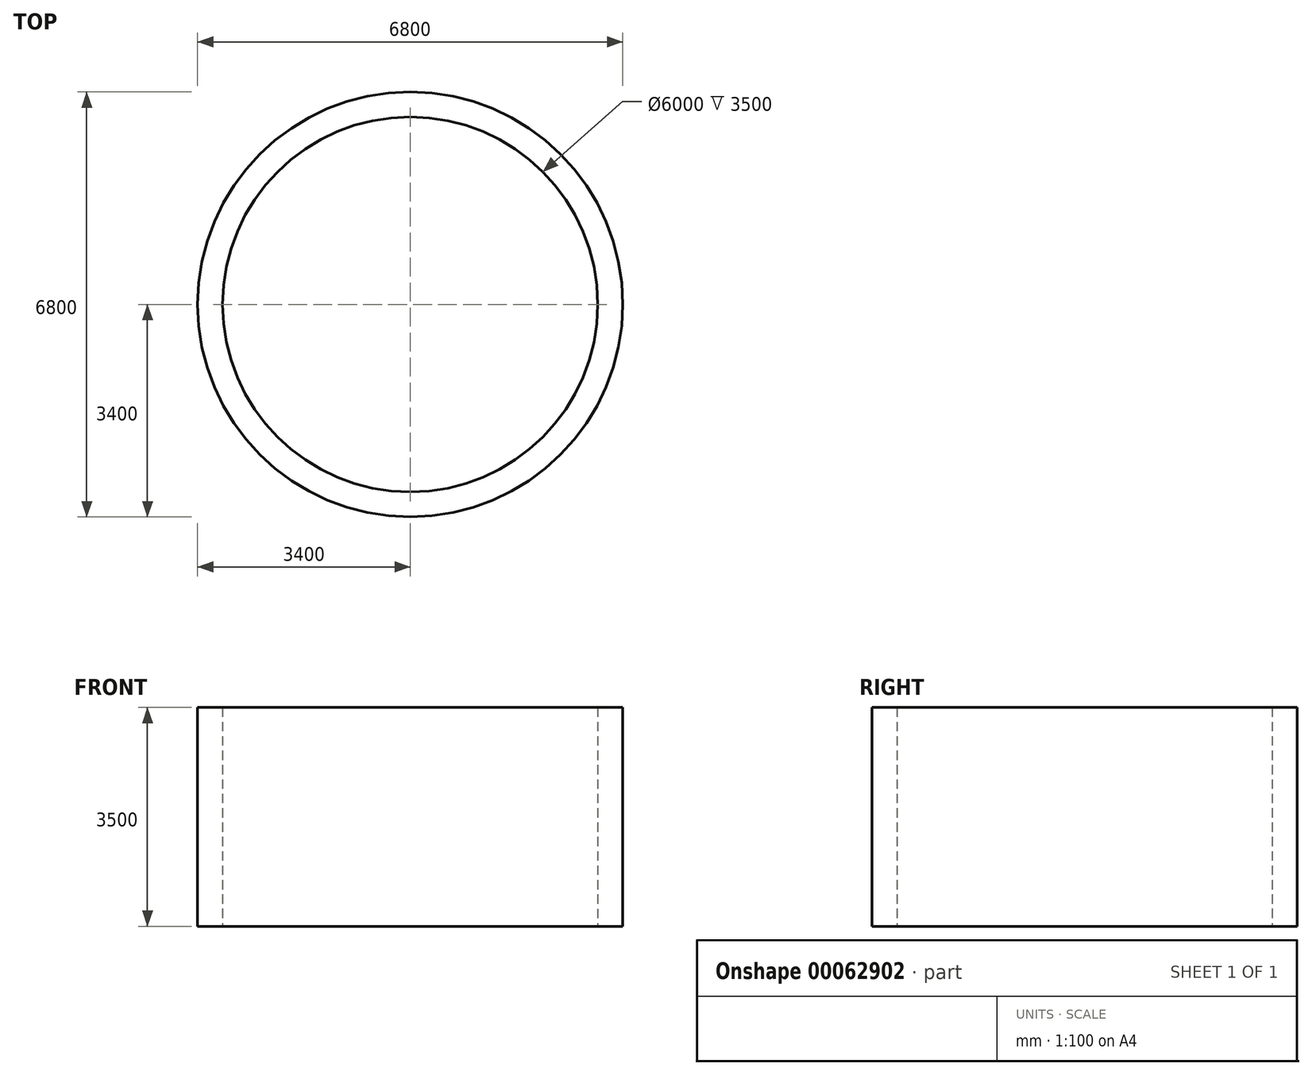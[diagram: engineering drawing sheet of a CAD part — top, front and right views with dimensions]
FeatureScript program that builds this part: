
annotation { "Feature Type Name" : "Feature", "Feature Type Description" : "" }
export const myFeature = defineFeature(function(context is Context, id is Id, definition is map)
    precondition{}
    {
        {
            var Q0;
            Q0=qCreatedBy(makeId("Top.planeOp"),FACE);
            var sketch = newSketch(context, id + "F0", { "sketchPlane" : qUnion([Q0])});
            skCircle(sketch, "E0", {"center": v(0, 0) * mm, "radius": 3000 * mm});
            skCircle(sketch, "E1.0", {"center": v(0, 0) * mm, "radius": 3400 * mm});
            skSolve(sketch);
        }
        {
            var Q0;
            Q0=makeQuery(id+"F0.imprint","IMPRINT",FACE,{"disambiguationData":[TD([[makeQuery(id+"F0.imprint","IMPRINT",EDGE,{"derivedFrom":sQuery(id+"F0.wireOp",EDGE,"E0")}),-1.0]])]});
            extrude(context, id + "F1", {"entities" : qUnion([Q0]), "depth" : 3500 * mm});
        }
    });
